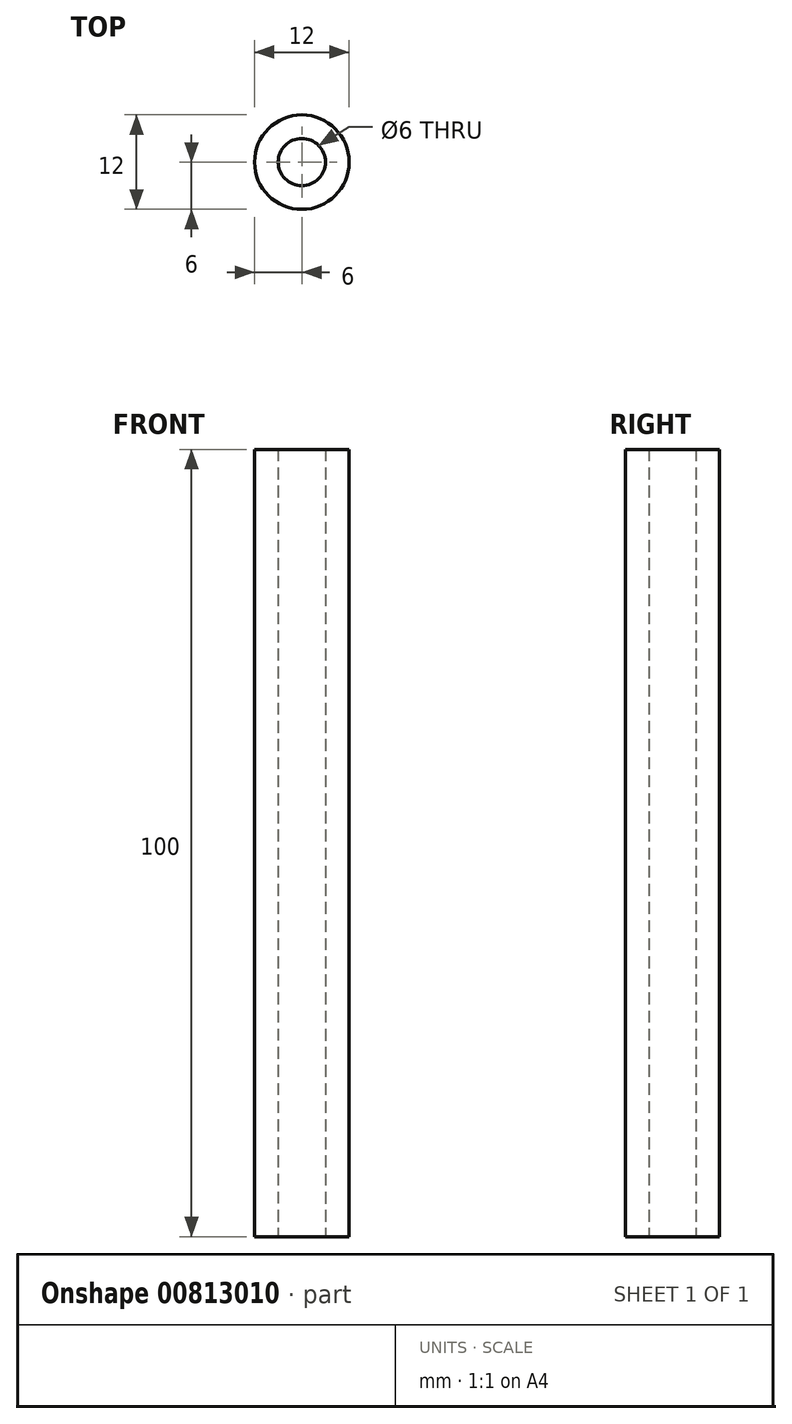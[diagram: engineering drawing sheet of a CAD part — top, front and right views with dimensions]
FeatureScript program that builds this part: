
annotation { "Feature Type Name" : "Feature", "Feature Type Description" : "" }
export const myFeature = defineFeature(function(context is Context, id is Id, definition is map)
    precondition{}
    {
        {
            var Q0;
            Q0=qCreatedBy(makeId("Top.planeOp"),FACE);
            var sketch = newSketch(context, id + "F0", { "sketchPlane" : qUnion([Q0])});
            skCircle(sketch, "E0", {"center": v(0, 0) * mm, "radius": 6 * mm});
            skCircle(sketch, "E1", {"center": v(0, 0) * mm, "radius": 3 * mm});
            skSolve(sketch);
        }
        {
            var Q0;
            Q0=makeQuery(id+"F0.imprint","IMPRINT",FACE,{"disambiguationData":[TD([[makeQuery(id+"F0.imprint","IMPRINT",EDGE,{"derivedFrom":sQuery(id+"F0.wireOp",EDGE,"E0")}),1.0]])]});
            extrude(context, id + "F1", {"entities" : qUnion([Q0]), "depth" : 100 * mm, "offsetDistance" : 25 * mm});
        }
    });
